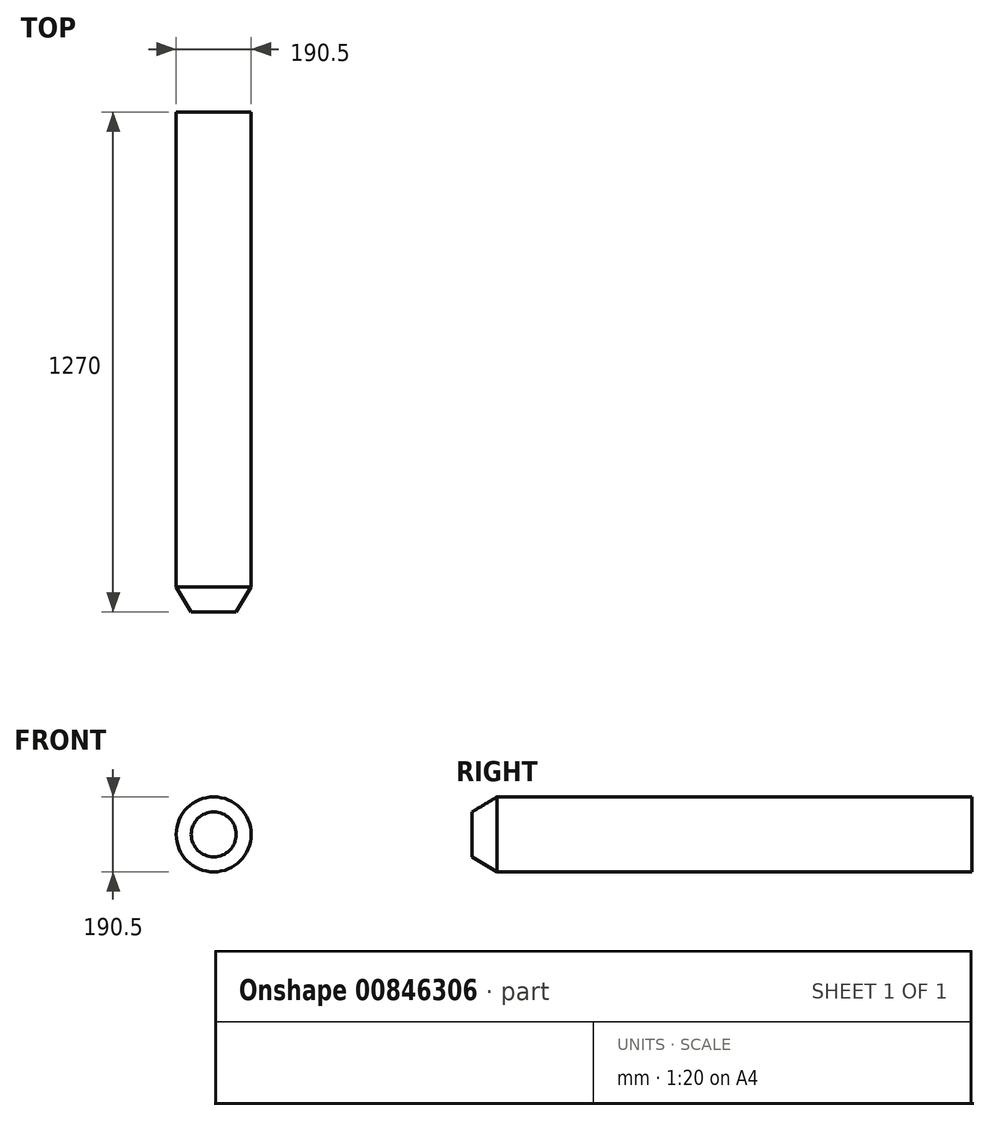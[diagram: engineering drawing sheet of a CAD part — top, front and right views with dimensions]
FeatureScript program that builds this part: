
annotation { "Feature Type Name" : "Feature", "Feature Type Description" : "" }
export const myFeature = defineFeature(function(context is Context, id is Id, definition is map)
    precondition{}
    {
        {
            var Q0;
            Q0=qCreatedBy(makeId("Right.planeOp"),FACE);
            var sketch = newSketch(context, id + "F0", { "sketchPlane" : qUnion([Q0])});
            skLineSegment(sketch, "E0", {"start": v(-1270, 0) * mm, "end": v(-1270, 57.15) * mm});
            skLineSegment(sketch, "E1", {"start": v(-1270, 57.15) * mm, "end": v(-1206.5, 95.25) * mm});
            skLineSegment(sketch, "E2", {"start": v(-1206.5, 95.25) * mm, "end": v(0, 95.25) * mm});
            skLineSegment(sketch, "E3", {"start": v(0, 95.25) * mm, "end": v(0, 0) * mm});
            skLineSegment(sketch, "E4", {"start": v(0, 0) * mm, "end": v(-1270, 0) * mm});
            skSolve(sketch);
        }
        {
            var Q0;
            Q0=makeQuery(id+"F0.imprint","IMPRINT",FACE,{"disambiguationData":[TD([[makeQuery(id+"F0.imprint","IMPRINT",EDGE,{"derivedFrom":sQuery(id+"F0.wireOp",EDGE,"E0")}),-1.0]])]});
            var Q1;
            Q1=sQuery(id+"F0.wireOp",EDGE,"E4");
            revolve(context, id + "F1", {"surfaceOperationType" : NewSurfaceOperationType.NEW, "entities" : qUnion([Q0]), "axis" : qUnion([Q1]), "revolveType" : RevolveType.FULL});
        }
    });
